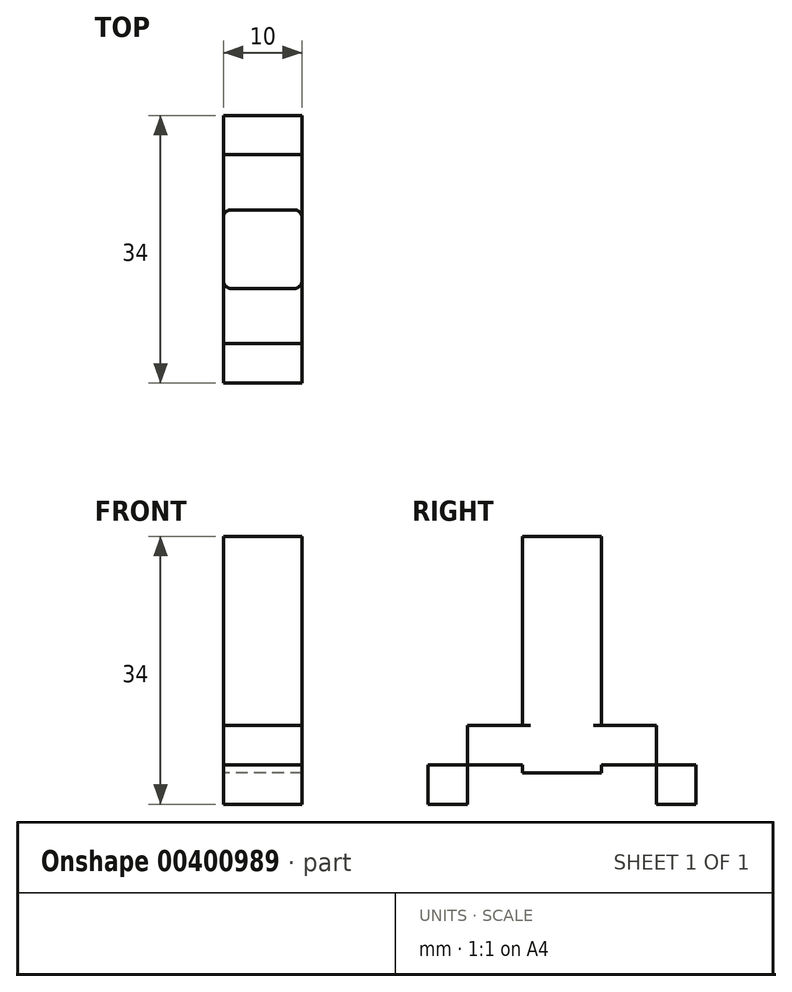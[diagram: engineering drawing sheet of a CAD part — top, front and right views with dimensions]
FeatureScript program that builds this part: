
annotation { "Feature Type Name" : "Feature", "Feature Type Description" : "" }
export const myFeature = defineFeature(function(context is Context, id is Id, definition is map)
    precondition{}
    {
        {
            var Q0;
            Q0=qCreatedBy(makeId("Right.planeOp"),FACE);
            var sketch = newSketch(context, id + "F0", { "sketchPlane" : qUnion([Q0])});
            skLineSegment(sketch, "E0.bottom", {"start": v(0, 0) * mm, "end": v(0, 0) * mm});
            skLineSegment(sketch, "E0.top", {"start": v(0, 0) * mm, "end": v(0, 0) * mm});
            skLineSegment(sketch, "E0.left", {"start": v(0, 0) * mm, "end": v(0, 0) * mm});
            skLineSegment(sketch, "E0.right", {"start": v(0, 0) * mm, "end": v(0, 0) * mm});
            skLineSegment(sketch, "E1.bottom", {"start": v(5, -15) * mm, "end": v(-5, -15) * mm});
            skLineSegment(sketch, "E1.top", {"start": v(5, 15) * mm, "end": v(-5, 15) * mm});
            skLineSegment(sketch, "E1.left", {"start": v(5, -15) * mm, "end": v(5, 15) * mm});
            skLineSegment(sketch, "E1.right", {"start": v(-5, -15) * mm, "end": v(-5, 15) * mm});
            skPoint(sketch, "E1.middle", {"position": v(0, 0) * mm});
            skLineSegment(sketch, "E2.bottom", {"start": v(17, -9) * mm, "end": v(-17, -9) * mm});
            skLineSegment(sketch, "E2.top", {"start": v(17, -14) * mm, "end": v(-17, -14) * mm});
            skLineSegment(sketch, "E2.left", {"start": v(17, -9) * mm, "end": v(17, -14) * mm});
            skLineSegment(sketch, "E2.right", {"start": v(-17, -9) * mm, "end": v(-17, -14) * mm});
            skPoint(sketch, "E2.middle", {"position": v(0, -11.5) * mm});
            skLineSegment(sketch, "E3.bottom", {"start": v(-12, -19) * mm, "end": v(-17, -19) * mm});
            skLineSegment(sketch, "E3.top", {"start": v(-12, -9) * mm, "end": v(-17, -9) * mm});
            skLineSegment(sketch, "E3.left", {"start": v(-12, -19) * mm, "end": v(-12, -9) * mm});
            skLineSegment(sketch, "E3.right", {"start": v(-17, -19) * mm, "end": v(-17, -9) * mm});
            skPoint(sketch, "E3.middle", {"position": v(-14.5, -14) * mm});
            skLineSegment(sketch, "E4.bottom", {"start": v(17, -19) * mm, "end": v(12, -19) * mm});
            skLineSegment(sketch, "E4.top", {"start": v(17, -9) * mm, "end": v(12, -9) * mm});
            skLineSegment(sketch, "E4.left", {"start": v(17, -19) * mm, "end": v(17, -9) * mm});
            skLineSegment(sketch, "E4.right", {"start": v(12, -19) * mm, "end": v(12, -9) * mm});
            skPoint(sketch, "E4.middle", {"position": v(14.5, -14) * mm});
            skSolve(sketch);
        }
        {
            var Q0;
            {var subQ0=sQuery(id+"F0.wireOp",EDGE,"E1.top");Q0=makeQuery(id+"F0.imprint","IMPRINT",FACE,{"disambiguationData":[TD([[makeQuery(id+"F0.imprint","IMPRINT",EDGE,{"derivedFrom":subQ0}),1.0]])]});}
            var Q1;
            {var subQ0=sQuery(id+"F0.wireOp",EDGE,"E2.top");var subQ1=sQuery(id+"F0.wireOp",EDGE,"E1.left");var subQ2=makeQuery(id+"F0.imprint","INTERSECT",VERTEX,{"derivedFrom":[subQ1,subQ0]});Q1=makeQuery(id+"F0.imprint","IMPRINT",FACE,{"disambiguationData":[TD([[makeQuery(id+"F0.imprint","IMPRINT",EDGE,{"disambiguationData":[TD([[subQ2,-1.0]])],"derivedFrom":subQ1}),1.0]])]});}
            var Q2;
            {var subQ0=sQuery(id+"F0.wireOp",EDGE,"E2.top");var subQ1=sQuery(id+"F0.wireOp",EDGE,"E1.left");var subQ2=makeQuery(id+"F0.imprint","INTERSECT",VERTEX,{"derivedFrom":[subQ1,subQ0]});Q2=makeQuery(id+"F0.imprint","IMPRINT",FACE,{"disambiguationData":[TD([[makeQuery(id+"F0.imprint","IMPRINT",EDGE,{"disambiguationData":[TD([[subQ2,-1.0]])],"derivedFrom":subQ1}),-1.0]])]});}
            var Q3;
            {var subQ5=sQuery(id+"F0.wireOp",EDGE,"E4.top");Q3=makeQuery(id+"F0.imprint","IMPRINT",FACE,{"disambiguationData":[TD([[makeQuery(id+"F0.imprint","IMPRINT",EDGE,{"derivedFrom":subQ5}),1.0]])]});}
            var Q4;
            {var subQ5=sQuery(id+"F0.wireOp",EDGE,"E4.bottom");Q4=makeQuery(id+"F0.imprint","IMPRINT",FACE,{"disambiguationData":[TD([[makeQuery(id+"F0.imprint","IMPRINT",EDGE,{"derivedFrom":subQ5}),-1.0]])]});}
            var Q5;
            {var subQ0=sQuery(id+"F0.wireOp",EDGE,"E2.top");var subQ1=sQuery(id+"F0.wireOp",EDGE,"E1.right");var subQ2=makeQuery(id+"F0.imprint","INTERSECT",VERTEX,{"derivedFrom":[subQ1,subQ0]});Q5=makeQuery(id+"F0.imprint","IMPRINT",FACE,{"disambiguationData":[TD([[makeQuery(id+"F0.imprint","IMPRINT",EDGE,{"disambiguationData":[TD([[subQ2,-1.0]])],"derivedFrom":subQ1}),1.0]])]});}
            var Q6;
            {var subQ5=sQuery(id+"F0.wireOp",EDGE,"E3.top");Q6=makeQuery(id+"F0.imprint","IMPRINT",FACE,{"disambiguationData":[TD([[makeQuery(id+"F0.imprint","IMPRINT",EDGE,{"derivedFrom":subQ5}),1.0]])]});}
            var Q7;
            {var subQ5=sQuery(id+"F0.wireOp",EDGE,"E3.bottom");Q7=makeQuery(id+"F0.imprint","IMPRINT",FACE,{"disambiguationData":[TD([[makeQuery(id+"F0.imprint","IMPRINT",EDGE,{"derivedFrom":subQ5}),-1.0]])]});}
            var Q8;
            {var subQ0=sQuery(id+"F0.wireOp",EDGE,"E1.bottom");Q8=makeQuery(id+"F0.imprint","IMPRINT",FACE,{"disambiguationData":[TD([[makeQuery(id+"F0.imprint","IMPRINT",EDGE,{"derivedFrom":subQ0}),-1.0]])]});}
            extrude(context, id + "F1", {"entities" : qUnion([Q0, Q1, Q2, Q3, Q4, Q5, Q6, Q7, Q8]), "depth" : 10 * mm});
        }
        {
            var Q0;
            {var subQ0=sQuery(id+"F0.wireOp",EDGE,"E1.left");Q0=makeQuery(id+"F1.opExtrude","CAP_EDGE",EDGE,{"disambiguationData":[OSD([subQ0]),TDD([makeQuery(id+"F0.imprint","IMPRINT",EDGE,{"disambiguationData":[TD([[makeQuery(id+"F0.imprint","INTERSECT",VERTEX,{"derivedFrom":[sQuery(id+"F0.wireOp",EDGE,"E1.top"),subQ0]}),1.0]])],"derivedFrom":subQ0})])],"isStart":true});}
            fillet(context, id + "F2", {"entities" : qUnion([Q0]), "radius" : 1 * mm, "tangentPropagation" : true, "allowEdgeOverflow" : false});
        }
        {
            var Q0;
            {var subQ0=sQuery(id+"F0.wireOp",EDGE,"E1.left");Q0=makeQuery(id+"F1.opExtrude","CAP_EDGE",EDGE,{"disambiguationData":[OSD([subQ0]),TDD([makeQuery(id+"F0.imprint","IMPRINT",EDGE,{"disambiguationData":[TD([[makeQuery(id+"F0.imprint","INTERSECT",VERTEX,{"derivedFrom":[sQuery(id+"F0.wireOp",EDGE,"E1.top"),subQ0]}),1.0]])],"derivedFrom":subQ0})])],"isStart":false});}
            fillet(context, id + "F3", {"entities" : qUnion([Q0]), "radius" : 1 * mm, "tangentPropagation" : true, "allowEdgeOverflow" : false});
        }
        {
            var Q0;
            {var subQ0=sQuery(id+"F0.wireOp",EDGE,"E1.right");Q0=makeQuery(id+"F1.opExtrude","CAP_EDGE",EDGE,{"disambiguationData":[OSD([subQ0]),TDD([makeQuery(id+"F0.imprint","IMPRINT",EDGE,{"disambiguationData":[TD([[makeQuery(id+"F0.imprint","INTERSECT",VERTEX,{"derivedFrom":[sQuery(id+"F0.wireOp",EDGE,"E1.top"),subQ0]}),1.0]])],"derivedFrom":subQ0})])],"isStart":true});}
            fillet(context, id + "F4", {"entities" : qUnion([Q0]), "radius" : 1 * mm, "tangentPropagation" : true, "allowEdgeOverflow" : false});
        }
        {
            var Q0;
            {var subQ0=sQuery(id+"F0.wireOp",EDGE,"E1.right");Q0=makeQuery(id+"F1.opExtrude","CAP_EDGE",EDGE,{"disambiguationData":[OSD([subQ0]),TDD([makeQuery(id+"F0.imprint","IMPRINT",EDGE,{"disambiguationData":[TD([[makeQuery(id+"F0.imprint","INTERSECT",VERTEX,{"derivedFrom":[sQuery(id+"F0.wireOp",EDGE,"E1.top"),subQ0]}),1.0]])],"derivedFrom":subQ0})])],"isStart":false});}
            fillet(context, id + "F5", {"entities" : qUnion([Q0]), "radius" : 1 * mm, "tangentPropagation" : true, "allowEdgeOverflow" : false});
        }
    });
